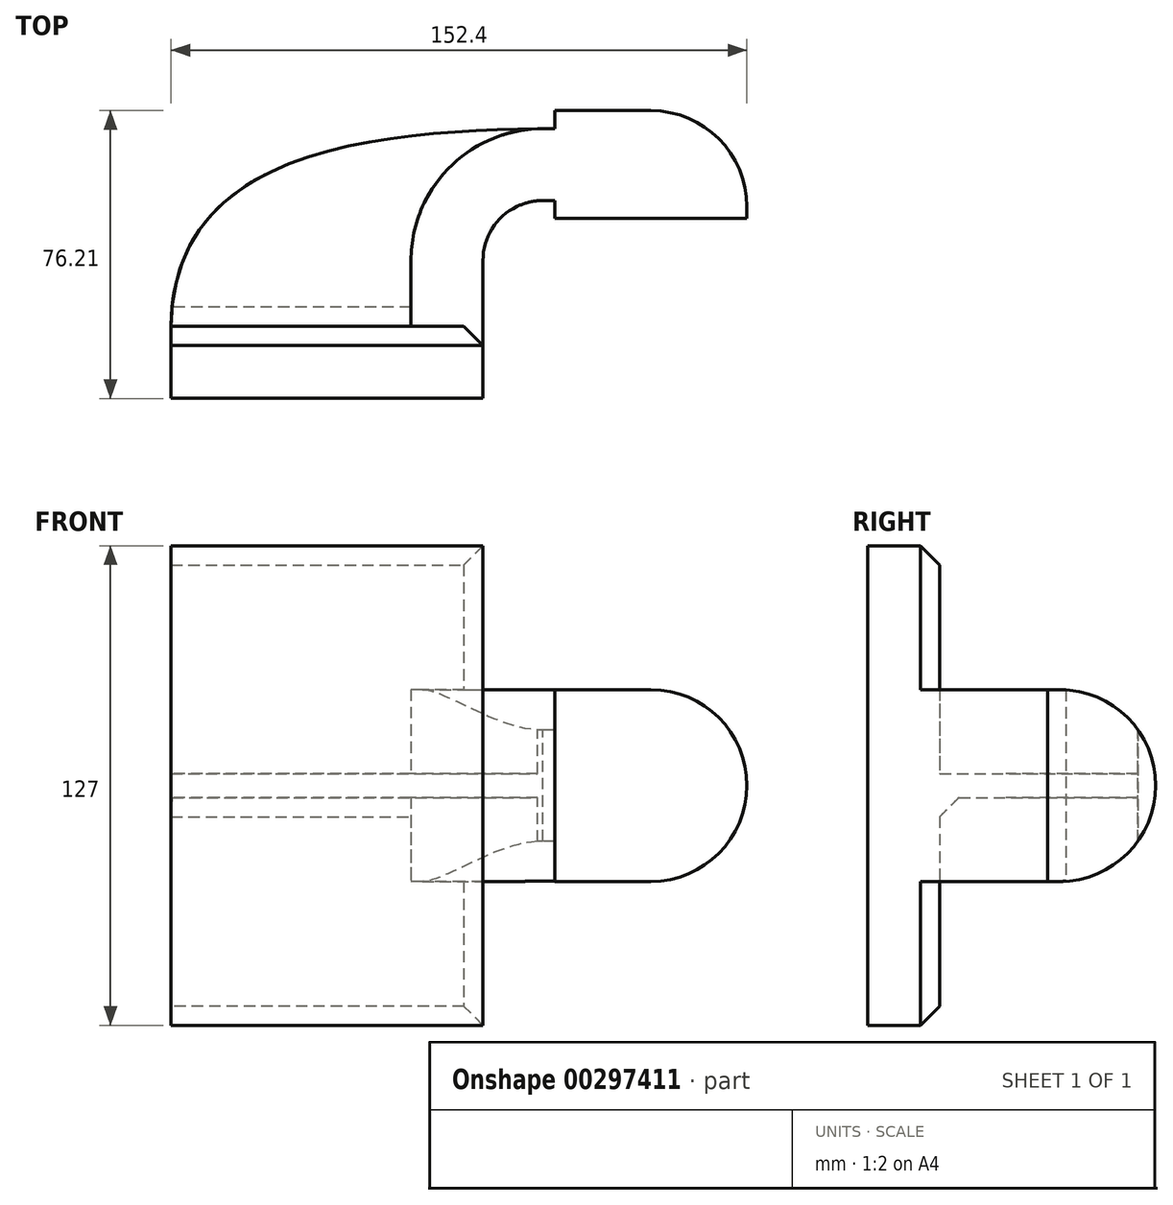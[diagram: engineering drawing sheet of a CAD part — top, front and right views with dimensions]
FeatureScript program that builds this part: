
annotation { "Feature Type Name" : "Feature", "Feature Type Description" : "" }
export const myFeature = defineFeature(function(context is Context, id is Id, definition is map)
    precondition{}
    {
        {
            var Q0;
            Q0=qCreatedBy(makeId("Top.planeOp"),FACE);
            var sketch = newSketch(context, id + "F0", { "sketchPlane" : qUnion([Q0])});
            skLineSegment(sketch, "E0.bottom", {"start": v(41.28, 9.53) * mm, "end": v(-41.28, 9.53) * mm});
            skLineSegment(sketch, "E0.top", {"start": v(41.28, -9.52) * mm, "end": v(-41.28, -9.52) * mm});
            skLineSegment(sketch, "E0.left", {"start": v(-41.28, 9.53) * mm, "end": v(-41.28, -9.52) * mm});
            skLineSegment(sketch, "E0.right", {"start": v(41.28, 9.53) * mm, "end": v(41.28, -9.53) * mm});
            skPoint(sketch, "E0.middle", {"position": v(0, 0) * mm});
            skLineSegment(sketch, "E1.bottom", {"start": v(60.33, 38.1) * mm, "end": v(111.13, 38.1) * mm});
            skLineSegment(sketch, "E1.top", {"start": v(60.33, 66.68) * mm, "end": v(111.13, 66.68) * mm});
            skLineSegment(sketch, "E1.left", {"start": v(60.33, 38.1) * mm, "end": v(60.33, 66.68) * mm});
            skLineSegment(sketch, "E1.right", {"start": v(111.13, 38.1) * mm, "end": v(111.13, 66.68) * mm});
            skPoint(sketch, "E1.middle", {"position": v(85.73, 52.39) * mm});
            skLineSegment(sketch, "E2", {"start": v(41.28, 9.53) * mm, "end": v(41.28, 27) * mm});
            skArc(sketch, "E3", {"start": v(41.27, 27) * mm, "mid": v(45.92, 38.23) * mm, "end": v(57.15, 42.88) * mm});
            skLineSegment(sketch, "E4", {"start": v(57.15, 42.88) * mm, "end": v(85.72, 42.88) * mm});
            skLineSegment(sketch, "E5.0", {"start": v(57.15, 61.93) * mm, "end": v(85.72, 61.93) * mm});
            skArc(sketch, "E5.1", {"start": v(22.22, 27) * mm, "mid": v(32.45, 51.7) * mm, "end": v(57.15, 61.93) * mm});
            skLineSegment(sketch, "E5.2", {"start": v(22.23, 9.53) * mm, "end": v(22.23, 27) * mm});
            skLineSegment(sketch, "E6", {"start": v(85.73, 38.1) * mm, "end": v(85.73, 66.68) * mm});
            skFitSpline(sketch, "E7", {"points": [v(-41.28, 9.53) * mm, v(57.15, 61.93) * mm], "startDerivative": vector(1.13, 146.92) * mm, "endDerivative": vector(119.38, 2.3) * mm});
            skSolve(sketch);
        }
        {
            var Q0;
            Q0=makeQuery(id+"F0.imprint","IMPRINT",FACE,{"disambiguationData":[TD([[makeQuery(id+"F0.imprint","IMPRINT",EDGE,{"derivedFrom":sQuery(id+"F0.wireOp",EDGE,"E0.top")}),-1.0]])]});
            extrude(context, id + "F1", {"entities" : qUnion([Q0]), "endBound" : BoundingType.SYMMETRIC, "depth" : 127 * mm});
        }
        {
            var Q0;
            {var subQ1=sQuery(id+"F0.wireOp",EDGE,"E2");Q0=makeQuery(id+"F0.imprint","IMPRINT",FACE,{"disambiguationData":[TD([[makeQuery(id+"F0.imprint","IMPRINT",EDGE,{"derivedFrom":subQ1}),1.0]])]});}
            var Q1;
            {var subQ0=sQuery(id+"F0.wireOp",EDGE,"E4");var subQ1=sQuery(id+"F0.wireOp",EDGE,"E1.left");var subQ2=makeQuery(id+"F0.imprint","INTERSECT",VERTEX,{"derivedFrom":[subQ1,subQ0]});Q1=makeQuery(id+"F0.imprint","IMPRINT",FACE,{"disambiguationData":[TD([[makeQuery(id+"F0.imprint","IMPRINT",EDGE,{"disambiguationData":[TD([[subQ2,-1.0]])],"derivedFrom":subQ1}),-1.0]])]});}
            var Q2;
            {var subQ0=sQuery(id+"F0.wireOp",EDGE,"E1.left");var subQ1=sQuery(id+"F0.wireOp",EDGE,"E1.bottom");var subQ2=makeQuery(id+"F0.imprint","INTERSECT",VERTEX,{"derivedFrom":[subQ1,subQ0]});Q2=makeQuery(id+"F0.imprint","IMPRINT",FACE,{"disambiguationData":[TD([[makeQuery(id+"F0.imprint","IMPRINT",EDGE,{"disambiguationData":[TD([[subQ2,-1.0]])],"derivedFrom":subQ1}),1.0]])]});}
            var Q3;
            {var subQ0=sQuery(id+"F0.wireOp",EDGE,"E1.left");var subQ1=sQuery(id+"F0.wireOp",EDGE,"E1.top");var subQ2=makeQuery(id+"F0.imprint","INTERSECT",VERTEX,{"derivedFrom":[subQ1,subQ0]});Q3=makeQuery(id+"F0.imprint","IMPRINT",FACE,{"disambiguationData":[TD([[makeQuery(id+"F0.imprint","IMPRINT",EDGE,{"disambiguationData":[TD([[subQ2,-1.0]])],"derivedFrom":subQ1}),-1.0]])]});}
            extrude(context, id + "F2", {"entities" : qUnion([Q0, Q1, Q2, Q3]), "operationType" : NewBodyOperationType.ADD, "endBound" : BoundingType.SYMMETRIC, "depth" : 50.8 * mm});
        }
        {
            var Q0;
            {var subQ3=sQuery(id+"F0.wireOp",EDGE,"E5.2");Q0=makeQuery(id+"F0.imprint","IMPRINT",FACE,{"disambiguationData":[TD([[makeQuery(id+"F0.imprint","IMPRINT",EDGE,{"derivedFrom":subQ3}),1.0]])]});}
            extrude(context, id + "F3", {"entities" : qUnion([Q0]), "operationType" : NewBodyOperationType.ADD, "endBound" : BoundingType.SYMMETRIC, "depth" : 6.35 * mm});
        }
        {
            var Q0;
            {var subQ4=sQuery(id+"F0.wireOp",EDGE,"E1.right");Q0=makeQuery(id+"F0.imprint","IMPRINT",FACE,{"disambiguationData":[TD([[makeQuery(id+"F0.imprint","IMPRINT",EDGE,{"derivedFrom":subQ4}),1.0]])]});}
            var Q1;
            Q1=sQuery(id+"F0.wireOp",EDGE,"E6");
            revolve(context, id + "F4", {"operationType" : NewBodyOperationType.ADD, "entities" : qUnion([Q0]), "axis" : qUnion([Q1]), "revolveType" : RevolveType.FULL});
        }
        {
            var Q0;
            Q0=makeQuery(id+"F4.opRevolve","SWEPT_EDGE",EDGE,{"disambiguationData":[OSD([sQuery(id+"F0.wireOp",EDGE,"E1.top"),sQuery(id+"F0.wireOp",EDGE,"E1.right")])]});
            fillet(context, id + "F5", {"entities" : qUnion([Q0]), "radius" : 25.4 * mm, "tangentPropagation" : true, "allowEdgeOverflow" : false});
        }
        {
            var Q0;
            Q0=makeQuery(id+"F3.opExtrude","CAP_EDGE",EDGE,{"disambiguationData":[OSD([sQuery(id+"F0.wireOp",EDGE,"E0.bottom")])],"isStart":false});
            var Q1;
            Q1=makeQuery(id+"F3.opExtrude","CAP_EDGE",EDGE,{"disambiguationData":[OSD([sQuery(id+"F0.wireOp",EDGE,"E0.bottom")])],"isStart":true});
            var Q2;
            Q2=makeQuery(id+"F1.opExtrude","CAP_EDGE",EDGE,{"disambiguationData":[OSD([sQuery(id+"F0.wireOp",EDGE,"E0.bottom")])],"isStart":true});
            var Q3;
            {var subQ0=sQuery(id+"F0.wireOp",EDGE,"E2");var subQ1=sQuery(id+"F0.wireOp",EDGE,"E0.bottom");var subQ2=sQuery(id+"F0.wireOp",EDGE,"E0.right");Q3=makeQuery(id+"F2.boolean.opBoolean","SPLIT",EDGE,{"disambiguationData":[TD([makeQuery(id+"F1.opExtrude","CAP_FACE",FACE,{"disambiguationData":[OSD([subQ1,sQuery(id+"F0.wireOp",EDGE,"E0.top"),sQuery(id+"F0.wireOp",EDGE,"E0.left"),subQ2])],"isStart":true})])],"derivedFrom":makeQuery(id+"F1.opExtrude","SWEPT_EDGE",EDGE,{"disambiguationData":[OSD([subQ1,subQ2,subQ0])]})});}
            var Q4;
            {var subQ0=sQuery(id+"F0.wireOp",EDGE,"E2");var subQ1=sQuery(id+"F0.wireOp",EDGE,"E0.bottom");var subQ2=sQuery(id+"F0.wireOp",EDGE,"E0.right");Q4=makeQuery(id+"F2.boolean.opBoolean","SPLIT",EDGE,{"disambiguationData":[TD([makeQuery(id+"F1.opExtrude","CAP_FACE",FACE,{"disambiguationData":[OSD([subQ1,sQuery(id+"F0.wireOp",EDGE,"E0.top"),sQuery(id+"F0.wireOp",EDGE,"E0.left"),subQ2])],"isStart":false})])],"derivedFrom":makeQuery(id+"F1.opExtrude","SWEPT_EDGE",EDGE,{"disambiguationData":[OSD([subQ1,subQ2,subQ0])]})});}
            var Q5;
            Q5=makeQuery(id+"F1.opExtrude","CAP_EDGE",EDGE,{"disambiguationData":[OSD([sQuery(id+"F0.wireOp",EDGE,"E0.bottom")])],"isStart":false});
            chamfer(context, id + "F6", {"entities" : qUnion([Q0, Q1, Q2, Q3, Q4, Q5]), "width" : 5.08 * mm, "tangentPropagation" : true});
        }
    });
